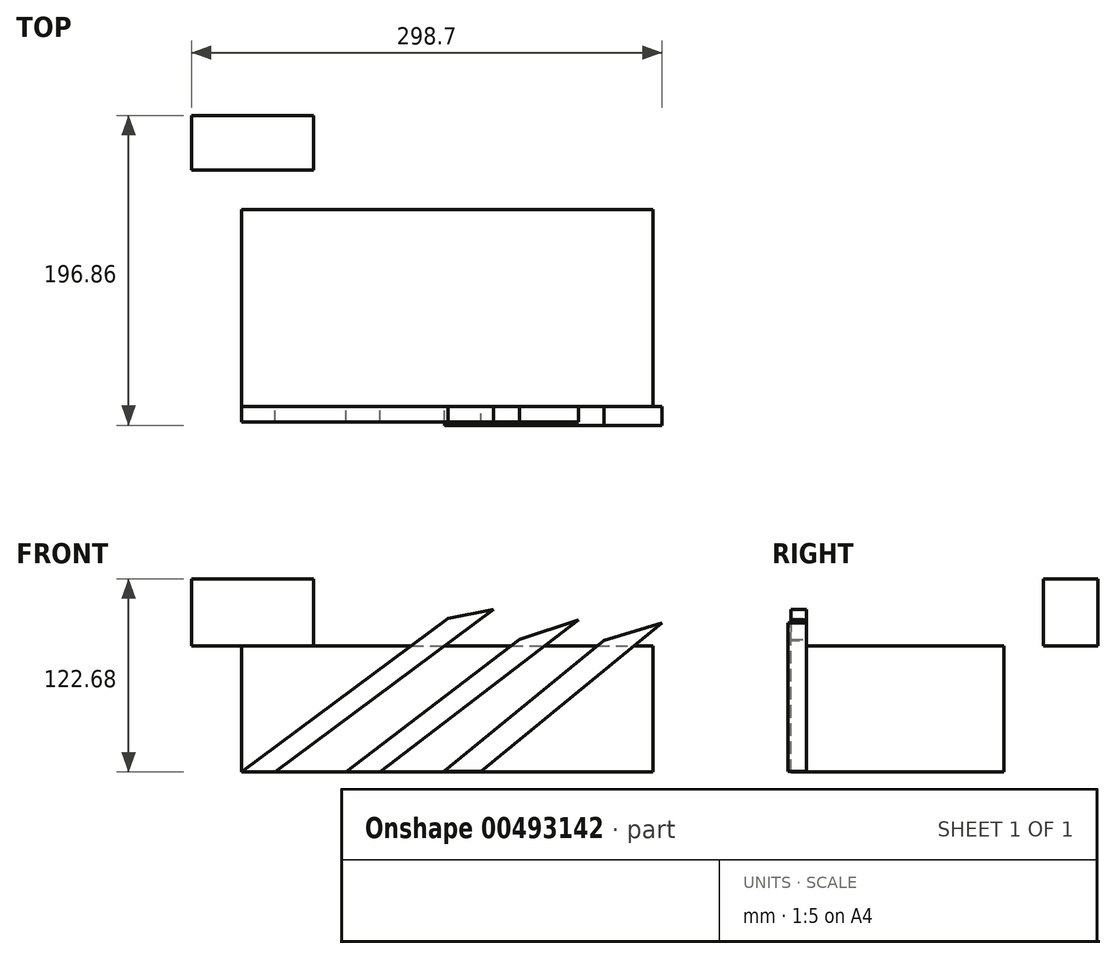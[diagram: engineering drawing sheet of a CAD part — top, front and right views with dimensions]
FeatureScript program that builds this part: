
annotation { "Feature Type Name" : "Feature", "Feature Type Description" : "" }
export const myFeature = defineFeature(function(context is Context, id is Id, definition is map)
    precondition{}
    {
        {
            var Q0;
            Q0=qCreatedBy(makeId("Top.planeOp"),FACE);
            var sketch = newSketch(context, id + "F0", { "sketchPlane" : qUnion([Q0])});
            skLineSegment(sketch, "E0.bottom", {"start": v(0, 0) * mm, "end": v(261.53, 0) * mm});
            skLineSegment(sketch, "E0.top", {"start": v(0, -125.25) * mm, "end": v(261.53, -125.25) * mm});
            skLineSegment(sketch, "E0.left", {"start": v(0, 0) * mm, "end": v(0, -125.25) * mm});
            skLineSegment(sketch, "E0.right", {"start": v(261.53, 0) * mm, "end": v(261.53, -125.25) * mm});
            skSolve(sketch);
        }
        {
            var Q0;
            Q0=makeQuery(id+"F0.imprint","IMPRINT",FACE,{"disambiguationData":[TD([[makeQuery(id+"F0.imprint","IMPRINT",EDGE,{"derivedFrom":sQuery(id+"F0.wireOp",EDGE,"E0.bottom")}),-1.0]])]});
            extrude(context, id + "F1", {"entities" : qUnion([Q0]), "oppositeDirection" : true, "depth" : 80.26 * mm});
        }
        {
            var Q0;
            Q0=qCreatedBy(makeId("Top.planeOp"),FACE);
            var sketch = newSketch(context, id + "F2", { "sketchPlane" : qUnion([Q0])});
            skLineSegment(sketch, "E1.bottom", {"start": v(-31.63, 59.67) * mm, "end": v(45.66, 59.67) * mm});
            skLineSegment(sketch, "E1.top", {"start": v(-31.63, 25.02) * mm, "end": v(45.66, 25.02) * mm});
            skLineSegment(sketch, "E1.left", {"start": v(-31.63, 59.67) * mm, "end": v(-31.63, 25.02) * mm});
            skLineSegment(sketch, "E1.right", {"start": v(45.66, 59.67) * mm, "end": v(45.66, 25.02) * mm});
            skSolve(sketch);
        }
        {
            var Q0;
            Q0=makeQuery(id+"F2.imprint","IMPRINT",FACE,{"disambiguationData":[TD([[makeQuery(id+"F2.imprint","IMPRINT",EDGE,{"derivedFrom":sQuery(id+"F2.wireOp",EDGE,"E1.bottom")}),-1.0]])]});
            extrude(context, id + "F3", {"entities" : qUnion([Q0]), "depth" : 42.42 * mm});
        }
        {
            var Q0;
            Q0=makeQuery(id+"F1.opExtrude","SWEPT_FACE",FACE,{"disambiguationData":[OSD([sQuery(id+"F0.wireOp",EDGE,"E0.top")])]});
            var sketch = newSketch(context, id + "F4", { "sketchPlane" : qUnion([Q0])});
            skLineSegment(sketch, "E2", {"start": v(0, -80.26) * mm, "end": v(131.35, 17.2) * mm});
            skLineSegment(sketch, "E3", {"start": v(21.24, -80.26) * mm, "end": v(160.24, 22.88) * mm});
            skLineSegment(sketch, "E4", {"start": v(66.45, -80.26) * mm, "end": v(176.56, 3.91) * mm});
            skLineSegment(sketch, "E5", {"start": v(87.93, -80.26) * mm, "end": v(214.14, 16.22) * mm});
            skLineSegment(sketch, "E6", {"start": v(214.14, 16.22) * mm, "end": v(176.56, 3.91) * mm});
            skLineSegment(sketch, "E7", {"start": v(160.24, 22.88) * mm, "end": v(131.35, 17.2) * mm});
            skSolve(sketch);
        }
        {
            var Q0;
            Q0 = qSketchRegion(id + "F4", true);
            var Q1;
            {var subQ1=sQuery(id+"F0.wireOp",EDGE,"E0.top");var subQ2=makeQuery(id+"F1.opExtrude","CAP_EDGE",EDGE,{"disambiguationData":[OSD([subQ1])],"isStart":false});var subQ6=sQuery(id+"F4.wireOp",EDGE,"E3");var subQ7=makeQuery(id+"F4.imprint","INTERSECT",VERTEX,{"derivedFrom":[subQ2,subQ6]});Q1=makeQuery(id+"F4.imprint","IMPRINT",FACE,{"disambiguationData":[TD([[makeQuery(id+"F4.imprint","IMPRINT",EDGE,{"disambiguationData":[TD([[subQ7,-1.0]])],"derivedFrom":subQ6}),1.0]])]});}
            extrude(context, id + "F5", {"entities" : qUnion([Q0, Q1]), "operationType" : NewBodyOperationType.ADD, "depth" : 9.9 * mm});
        }
        {
            var Q0;
            Q0 = qSketchRegion(id + "F4", true);
            var Q1;
            {var subQ0=sQuery(id+"F4.wireOp",EDGE,"E7");Q1=makeQuery(id+"F4.imprint","IMPRINT",FACE,{"disambiguationData":[TD([[makeQuery(id+"F4.imprint","IMPRINT",EDGE,{"derivedFrom":subQ0}),1.0]])]});}
            var Q2;
            {var subQ0=sQuery(id+"F4.wireOp",EDGE,"E4");var subQ1=sQuery(id+"F0.wireOp",EDGE,"E0.top");var subQ2=makeQuery(id+"F1.opExtrude","CAP_EDGE",EDGE,{"disambiguationData":[OSD([subQ1])],"isStart":false});var subQ3=makeQuery(id+"F4.imprint","INTERSECT",VERTEX,{"derivedFrom":[subQ2,subQ0]});Q2=makeQuery(id+"F4.imprint","IMPRINT",FACE,{"disambiguationData":[TD([[makeQuery(id+"F4.imprint","IMPRINT",EDGE,{"disambiguationData":[TD([[subQ3,-1.0]])],"derivedFrom":subQ0}),-1.0]])]});}
            var Q3;
            {var subQ0=sQuery(id+"F4.wireOp",EDGE,"E6");Q3=makeQuery(id+"F4.imprint","IMPRINT",FACE,{"disambiguationData":[TD([[makeQuery(id+"F4.imprint","IMPRINT",EDGE,{"derivedFrom":subQ0}),1.0]])]});}
            extrude(context, id + "F6", {"entities" : qUnion([Q0, Q1, Q2, Q3]), "operationType" : NewBodyOperationType.ADD, "depth" : 9.9 * mm});
        }
        {
            var Q0;
            {var subQ1=sQuery(id+"F0.wireOp",EDGE,"E0.top");var subQ6=makeQuery(id+"F1.opExtrude","SWEPT_EDGE",EDGE,{"disambiguationData":[OSD([subQ1,sQuery(id+"F0.wireOp",EDGE,"E0.right")])]});Q0=makeQuery(id+"F4.imprint","IMPRINT",FACE,{"disambiguationData":[TD([[makeQuery(id+"F4.imprint","IMPRINT",EDGE,{"derivedFrom":subQ6}),1.0]])]});}
            var sketch = newSketch(context, id + "F7", { "sketchPlane" : qUnion([Q0])});
            skLineSegment(sketch, "E8", {"start": v(129.1, -79.53) * mm, "end": v(230.44, 3.42) * mm});
            skLineSegment(sketch, "E9", {"start": v(152.04, -79.73) * mm, "end": v(267.07, 14.43) * mm});
            skLineSegment(sketch, "E10", {"start": v(267.07, 14.43) * mm, "end": v(230.44, 3.42) * mm});
            skLineSegment(sketch, "E11", {"start": v(129.1, -79.53) * mm, "end": v(152.04, -79.73) * mm});
            skSolve(sketch);
        }
        {
            var Q0;
            {var subQ0=sQuery(id+"F7.wireOp",EDGE,"E10");Q0=makeQuery(id+"F7.imprint","IMPRINT",FACE,{"disambiguationData":[TD([[makeQuery(id+"F7.imprint","IMPRINT",EDGE,{"derivedFrom":subQ0}),1.0]])]});}
            var Q1;
            {var subQ0=sQuery(id+"F7.wireOp",EDGE,"E11");Q1=makeQuery(id+"F7.imprint","IMPRINT",FACE,{"disambiguationData":[TD([[makeQuery(id+"F7.imprint","IMPRINT",EDGE,{"derivedFrom":subQ0}),1.0]])]});}
            extrude(context, id + "F8", {"entities" : qUnion([Q0, Q1]), "operationType" : NewBodyOperationType.ADD, "depth" : 11.94 * mm});
        }
    });
